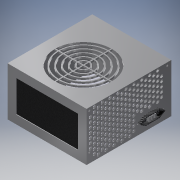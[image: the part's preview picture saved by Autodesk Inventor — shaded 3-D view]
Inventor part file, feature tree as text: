
AUTODESK INVENTOR PART (.ipt)
format: ipt  version: 2018.3 (Build 223284000, 284)  size: 2,143,232 bytes
history: native  units: mm
features: other x10, extrude x9, sketch x9, shell x1
ambient origin geometry x8: Origin, YZ Plane, XZ Plane, XY Plane, X Axis, Y Axis, Z Axis, Center Point
bodies: Solido1 (feature_tree)
feature tree (29):
  extrude  "Estrusione1"  Depth=140.0mm
  shell  "Svuotamento1"  Thickness=0.0mm
  extrude  "Estrusione2"  Depth=150.0mm
  extrude  "Estrusione3"  Depth=86.0mm TaperAngle=0.0deg
  extrude  "Estrusione4"  Depth=3.0mm
  extrude  "Estrusione5"  Depth=15.0mm
  extrude  "Estrusione6"  Depth=3.0mm TaperAngle=0.0deg
  extrude  "Estrusione7"  Depth=3.0mm
  extrude  "Estrusione8"  Depth=100.0mm
  extrude  "Estrusione9"  Depth=20.0mm
  sketch  "Schizzo1"
  sketch  "Schizzo3"
  other  "Linea chiusa proiettata1"
  sketch  "Schizzo4"
  sketch  "Schizzo5"
  other  "Linea chiusa proiettata2"
  sketch  "Schizzo6"
  sketch  "Schizzo7"
  other  "Linea chiusa proiettata3"
  other  "Linea chiusa proiettata4"
  other  "Linea chiusa proiettata5"
  other  "Linea chiusa proiettata6"
  sketch  "Schizzo8"
  sketch  "Schizzo9"
  sketch  "Schizzo10"
  other  "Linea chiusa proiettata7"
  other  "Proietta spigoli di taglio1"
  other  "Proietta spigoli di taglio2"
  other  "Proietta spigoli di taglio3"
